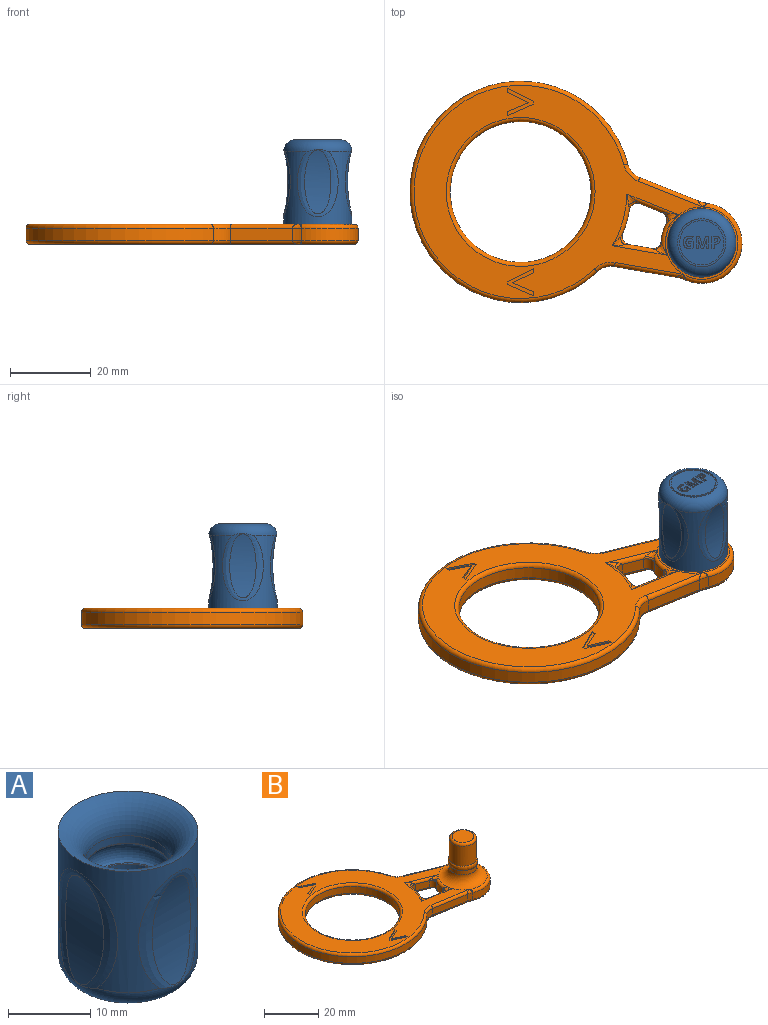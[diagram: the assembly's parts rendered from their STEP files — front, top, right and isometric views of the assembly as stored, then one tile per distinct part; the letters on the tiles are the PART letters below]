
ASSEMBLY  parts=2 mates=1
PART A: 79 faces, bbox 21x21x21.2 mm
  f0: cylinder r=5.2mm len=10.4mm, axis (0,0,1), area 36mm2, adj f14,f16
  f1: cylinder r=8.5mm len=18mm, axis (0,0,-1), area 388.7mm2, adj f6,f7,f8,f9,f10,f16
  f2: cylinder r=32.5mm len=15.91mm, axis (0,-1,0), area 83.7mm2, adj f6
  f3: cylinder r=32.5mm len=15.91mm, axis (0,-1,0), area 83.9mm2, adj f8
  f4: cylinder r=32.5mm len=15.92mm, axis (-1,0,0), area 83.9mm2, adj f7
  f5: cylinder r=32.5mm len=15.91mm, axis (-1,0,0), area 83.7mm2, adj f10
  f6: bspline ~17.38x10.13mm, area 57.8mm2, adj f1,f2,f9
  f7: bspline ~17.38x10.12mm, area 57.8mm2, adj f1,f4,f9
  f8: bspline ~17.38x10.12mm, area 58.2mm2, adj f1,f3,f9
  f9: torus R=5.5mm, axis (0,0,1), area 193.4mm2, adj f1,f6,f7,f8,f10,f18
  f10: bspline ~17.38x10.14mm, area 57.8mm2, adj f1,f5,f9
  f11: revolved ~11.8x11.8mm, area 116.4mm2, adj f14,f15
  f12: plane 10.4x10.4mm, normal (0,0,1), area 84.9mm2, adj f13
  f13: cylinder r=5.2mm len=10.45mm, axis (0,0,1), area 341.3mm2, adj f12,f15
  f14: torus R=5.35mm, axis (0,0,1), area 5.3mm2, adj f0,f11
  f15: torus R=5.35mm, axis (0,0,-1), area 5.3mm2, adj f11,f13
  f16: torus R=9.7mm, axis (0,0,1), area 234.1mm2, adj f0,f1
  f17: cylinder r=5.5mm len=11mm, axis (0,0,-1), area 13.8mm2, adj f19,f20
  f18: cylinder r=6mm len=12mm, axis (0,0,-1), area 13.5mm2, adj f9,f19
  f19: plane 12x12mm, normal (0,0,-1), area 18.1mm2, adj f17,f18
  f20: plane 11x11mm, normal (0,0,-1), area 80.4mm2, adj f17,f21,f22,f23,f24,f25,f26,f27
  f21: plane 1.18x0.4mm, normal (0,1,0), area 0.5mm2, adj f20,f22,f39,f40
  f22: plane 0.53x0.4mm, normal (1,0,0), area 0.2mm2, adj f20,f21,f23,f40
  f23: plane 0.56x0.4mm, normal (0,-1,0), area 0.2mm2, adj f20,f22,f24,f40
  f24: plane 0.62x0.4mm, normal (1,0,0), area 0.2mm2, adj f20,f23,f25,f40
  f25: extruded ~0.4x0.4mm, area 0.2mm2, adj f20,f24,f26,f40
  f26: extruded ~0.58x0.4mm, area 0.3mm2, adj f20,f25,f27,f40
  f27: extruded ~0.74x0.4mm, area 0.3mm2, adj f20,f26,f28,f40
  f28: extruded ~0.74x0.4mm, area 0.3mm2, adj f20,f27,f29,f40
  f29: extruded ~0.66x0.4mm, area 0.3mm2, adj f20,f28,f30,f40
  f30: extruded ~0.68x0.4mm, area 0.3mm2, adj f20,f29,f31,f40
  f31: plane 0.5x0.4mm, normal (-0.92,-0.38,0), area 0.2mm2, adj f20,f30,f32,f40
  f32: extruded ~0.88x0.4mm, area 0.4mm2, adj f20,f31,f33,f40
  f33: extruded ~1.14x0.4mm, area 0.5mm2, adj f20,f32,f34,f40
  f34: extruded ~1.12x0.41mm, area 0.5mm2, adj f20,f33,f35,f40
  f35: extruded ~1.14x0.4mm, area 0.5mm2, adj f20,f34,f36,f40
  f36: extruded ~1.03x0.4mm, area 0.5mm2, adj f20,f35,f37,f40
  f37: extruded ~0.52x0.4mm, area 0.2mm2, adj f20,f36,f38,f40
  f38: extruded ~0.54x0.4mm, area 0.2mm2, adj f20,f37,f39,f40
  f39: plane 1.54x0.4mm, normal (-1,0,0), area 0.6mm2, adj f20,f21,f38,f40
  f40: plane 3.06x2.44mm, normal (0,0,-1), area 4.3mm2, adj f21,f22,f23,f24,f25,f26,f27,f28
  f41: plane 2.33x0.72mm, normal (0.96,-0.29,0), area 1mm2, adj f20,f42,f59,f60
  f42: plane 0.58x0.4mm, normal (0,-1,0), area 0.2mm2, adj f20,f41,f43,f60
  f43: plane 2.33x0.77mm, normal (-0.95,-0.31,0), area 1mm2, adj f20,f42,f44,f60
  f44: plane 0.4x0.02mm, normal (0,-1,0), area 0mm2, adj f20,f43,f45,f60
  f45: extruded ~0.69x0.4mm, area 0.3mm2, adj f20,f44,f46,f60
  f46: extruded ~0.4x0.23mm, area 0.1mm2, adj f20,f45,f47,f60
  f47: plane 1.41x0.4mm, normal (1,0,0), area 0.6mm2, adj f20,f46,f48,f60
  f48: plane 0.59x0.4mm, normal (0,-1,0), area 0.2mm2, adj f20,f47,f49,f60
  f49: plane 2.97x0.4mm, normal (-1,0,0), area 1.2mm2, adj f20,f48,f50,f60
  f50: plane 0.86x0.4mm, normal (0,1,0), area 0.3mm2, adj f20,f49,f51,f60
  f51: plane 2.27x0.75mm, normal (0.95,0.31,0), area 1mm2, adj f20,f50,f52,f60
  f52: plane 0.4x0.01mm, normal (0,1,0), area 0mm2, adj f20,f51,f53,f60
  f53: plane 2.27x0.7mm, normal (-0.96,0.3,0), area 1mm2, adj f20,f52,f54,f60
  f54: plane 0.86x0.4mm, normal (0,1,0), area 0.3mm2, adj f20,f53,f55,f60
  f55: plane 2.97x0.4mm, normal (1,0,0), area 1.2mm2, adj f20,f54,f56,f60
  f56: plane 0.56x0.4mm, normal (0,-1,0), area 0.2mm2, adj f20,f55,f57,f60
  f57: plane 1.38x0.4mm, normal (-1,0,0), area 0.6mm2, adj f20,f56,f58,f60
  f58: extruded ~0.95x0.4mm, area 0.4mm2, adj f20,f57,f59,f60
  f59: plane 0.4x0.02mm, normal (0,-1,0), area 0mm2, adj f20,f41,f58,f60
  f60: plane 3.18x2.97mm, normal (0,0,-1), area 6.1mm2, adj f41,f42,f43,f44,f45,f46,f47,f48
  f61: extruded ~0.73x0.4mm, area 0.3mm2, adj f20,f62,f76,f77
  f62: extruded ~0.69x0.4mm, area 0.3mm2, adj f20,f61,f63,f77
  f63: extruded ~0.82x0.4mm, area 0.3mm2, adj f20,f62,f64,f77
  f64: plane 0.95x0.4mm, normal (0,1,0), area 0.4mm2, adj f20,f63,f65,f77
  f65: plane 2.97x0.4mm, normal (1,0,0), area 1.2mm2, adj f20,f64,f66,f77
  f66: plane 0.63x0.4mm, normal (0,-1,0), area 0.3mm2, adj f20,f65,f67,f77
  f67: plane 1.06x0.4mm, normal (-1,0,0), area 0.4mm2, adj f20,f66,f68,f77
  f68: plane 0.4x0.27mm, normal (0,-1,0), area 0.1mm2, adj f20,f67,f76,f77
  f69: plane 0.4x0.21mm, normal (0,1,0), area 0.1mm2, adj f70,f75,f77,f78
  f70: plane 0.88x0.4mm, normal (-1,0,0), area 0.4mm2, adj f69,f71,f77,f78
  f71: plane 0.4x0.29mm, normal (0,-1,0), area 0.1mm2, adj f70,f72,f77,f78
  f72: extruded ~0.4x0.38mm, area 0.2mm2, adj f71,f73,f77,f78
  f73: extruded ~0.4x0.33mm, area 0.1mm2, adj f72,f74,f77,f78
  f74: extruded ~0.4x0.33mm, area 0.2mm2, adj f73,f75,f77,f78
  f75: extruded ~0.44x0.4mm, area 0.2mm2, adj f69,f74,f77,f78
  f76: extruded ~0.85x0.4mm, area 0.4mm2, adj f20,f61,f68,f77
  f77: plane 2.97x2.05mm, normal (0,0,-1), area 3.6mm2, adj f61,f62,f63,f64,f65,f66,f67,f68
  f78: plane 0.88x0.79mm, normal (0,0,-1), area 0.6mm2, adj f69,f70,f71,f72,f73,f74,f75
PART B: 88 faces, bbox 87.6x59.5x23 mm
  f0: cylinder r=5mm len=13mm, axis (0,0,-1), area 394.6mm2, adj f24,f25,f86,f87
  f1: plane 71.67x53mm, normal (0,0,1), area 1242.5mm2, adj f24,f37,f39,f40,f41,f42,f43,f44
  f2: bspline ~2.83x2.45mm, area 2.5mm2, adj f34,f36,f61,f62
  f3: bspline ~2.83x2.45mm, area 2.5mm2, adj f45,f47,f62,f63
  f4: bspline ~2.54x2.25mm, area 1.8mm2, adj f35,f36,f58,f59
  f5: bspline ~2.54x2.25mm, area 1.8mm2, adj f46,f47,f59,f60
  f6: bspline ~2.81x2.09mm, area 1.8mm2, adj f33,f35,f55,f56
  f7: bspline ~2.81x2.09mm, area 1.8mm2, adj f44,f46,f56,f57
  f8: bspline ~2.86x2.45mm, area 2.5mm2, adj f33,f34,f52,f53
  f9: bspline ~2.86x2.45mm, area 2.5mm2, adj f44,f45,f53,f54
  f10: plane 45x45mm, normal (0,0,-1), area 511.7mm2, adj f32,f48,f49
  f11: cylinder r=10mm len=19.9mm, axis (0,0,-1), area 102.5mm2, adj f27,f38,f65,f68
  f12: plane 14.46x5.78mm, normal (0.37,0.93,0), area 46.7mm2, adj f13,f26,f37,f68
  f13: cylinder r=5mm len=3.38mm, axis (0,0,-1), area 14mm2, adj f12,f14,f28,f39
  f14: cylinder r=27.5mm len=55mm, axis (0,0,-1), area 430.7mm2, adj f13,f15,f30,f41
  f15: cylinder r=5mm len=4.31mm, axis (0,0,-1), area 14mm2, adj f14,f21,f31,f42
  f16: cylinder r=27.4mm len=5.86mm, axis (0,0,-1), area 18.3mm2, adj f34,f45,f53,f62
  f17: plane 5.36x3mm, normal (-0.37,-0.93,0), area 17.3mm2, adj f33,f44,f53,f56
  f18: cylinder r=10.1mm len=4.28mm, axis (0,0,-1), area 13.5mm2, adj f35,f46,f56,f59
  f19: cylinder r=17.5mm len=35mm, axis (0,0,-1), area 329.9mm2, adj f32,f43
  f20: plane 5.69x3mm, normal (0.17,0.99,0), area 17.3mm2, adj f36,f47,f59,f62
  f21: plane 15.34x3mm, normal (-0.17,-0.99,0), area 46.7mm2, adj f15,f29,f40,f65
  f22: plane 80.5x53mm, normal (0,0,-1), area 709.7mm2, adj f26,f27,f28,f29,f30,f31,f33,f34
  f23: plane 8x8mm, normal (0,0,1), area 50.3mm2, adj f25
  f24: torus R=9mm, axis (0,0,1), area 254.8mm2, adj f0,f1,f38
  f25: torus R=4mm, axis (0,0,1), area 45.8mm2, adj f0,f23
  f26: cylinder r=1mm len=16.32mm, axis (-0.93,0.37,0), area 25.7mm2, adj f12,f22,f28,f67
  f27: torus R=9mm, axis (0,0,1), area 53.5mm2, adj f11,f22,f64,f67
  f28: torus R=6mm, axis (0,0,1), area 7.9mm2, adj f13,f22,f26,f30
  f29: cylinder r=1mm len=17.1mm, axis (0.99,-0.17,0), area 25.7mm2, adj f21,f22,f31,f64
  f30: torus R=26.5mm, axis (0,0,1), area 222.5mm2, adj f14,f22,f28,f31
  f31: torus R=6mm, axis (0,0,1), area 7.9mm2, adj f15,f22,f29,f30
  f32: torus R=18.5mm, axis (0,0,1), area 176.3mm2, adj f10,f19
  f33: cylinder r=1mm len=13.23mm, axis (0.93,-0.37,0), area 13.9mm2, adj f6,f8,f17,f22,f52,f55
  f34: torus R=26.4mm, axis (0,0,1), area 14.1mm2, adj f2,f8,f16,f22,f52,f61
  f35: torus R=9.1mm, axis (0,0,1), area 11.1mm2, adj f4,f6,f18,f22,f55,f58
  f36: cylinder r=1mm len=13.82mm, axis (-0.99,0.17,0), area 13.9mm2, adj f2,f4,f20,f22,f58,f61
  f37: cylinder r=1mm len=16.32mm, axis (0.93,-0.37,0), area 25.7mm2, adj f1,f12,f39,f69
  f38: torus R=9mm, axis (0,0,1), area 53.5mm2, adj f11,f24,f66,f69
  f39: torus R=6mm, axis (0,0,1), area 7.9mm2, adj f1,f13,f37,f41
  f40: cylinder r=1mm len=17.1mm, axis (-0.99,0.17,0), area 25.7mm2, adj f1,f21,f42,f66
  f41: torus R=26.5mm, axis (0,0,1), area 222.5mm2, adj f1,f14,f39,f42
  f42: torus R=6mm, axis (0,0,1), area 7.9mm2, adj f1,f15,f40,f41
  f43: torus R=18.5mm, axis (0,0,1), area 176.3mm2, adj f1,f19
  f44: cylinder r=1mm len=13.23mm, axis (-0.93,0.37,0), area 13.9mm2, adj f1,f7,f9,f17,f54,f57
  f45: torus R=26.4mm, axis (0,0,1), area 14.1mm2, adj f1,f3,f9,f16,f54,f63
  f46: torus R=9.1mm, axis (0,0,1), area 11.1mm2, adj f1,f5,f7,f18,f57,f60
  f47: cylinder r=1mm len=13.82mm, axis (0.99,-0.17,0), area 13.9mm2, adj f1,f3,f5,f20,f60,f63
  f48: cylinder r=22.5mm len=45mm, axis (0,0,-1), area 276.7mm2, adj f10,f49,f51
  f49: cylinder r=1.5mm len=2.97mm, axis (0,0,-1), area 9.2mm2, adj f10,f48,f51
  f50: cylinder r=24.5mm len=49mm, axis (0,0,-1), area 307.9mm2, adj f22,f51
  f51: plane 49x49mm, normal (0,0,-1), area 298.8mm2, adj f48,f49,f50
  f52: bspline ~3.14x2.66mm, area 1.9mm2, adj f8,f33,f34
  f53: cylinder r=2mm len=3mm, axis (0,0,-1), area 10.7mm2, adj f8,f9,f16,f17
  f54: bspline ~3.14x2.66mm, area 1.9mm2, adj f9,f44,f45
  f55: bspline ~3.64x2.48mm, area 2.2mm2, adj f6,f33,f35
  f56: cylinder r=2mm len=3mm, axis (0,0,-1), area 10.1mm2, adj f6,f7,f17,f18
  f57: bspline ~3.64x2.48mm, area 2.2mm2, adj f7,f44,f46
  f58: bspline ~3.38x3.13mm, area 2.2mm2, adj f4,f35,f36
  f59: cylinder r=2mm len=3mm, axis (0,0,-1), area 10.1mm2, adj f4,f5,f18,f20
  f60: bspline ~3.38x3.13mm, area 2.2mm2, adj f5,f46,f47
  f61: bspline ~3.26x2.39mm, area 1.9mm2, adj f2,f34,f36
  f62: cylinder r=2mm len=3mm, axis (0,0,-1), area 10.7mm2, adj f2,f3,f16,f20
  f63: bspline ~3.26x2.39mm, area 1.9mm2, adj f3,f45,f47
  f64: bspline ~2.31x1.41mm, area 1.6mm2, adj f27,f29,f65
  f65: cylinder r=10mm len=3mm, axis (0,0,-1), area 7.3mm2, adj f11,f21,f64,f66
  f66: bspline ~2.31x1.41mm, area 1.6mm2, adj f38,f40,f65
  f67: bspline ~2.34x1.53mm, area 2.7mm2, adj f26,f27,f68
  f68: cylinder r=10mm len=3mm, axis (0,0,-1), area 7.3mm2, adj f11,f12,f67,f69
  f69: bspline ~2.34x1.53mm, area 1.6mm2, adj f37,f38,f68
  f70: plane 5.31x2.21mm, normal (0.38,-0.92,0), area 2.3mm2, adj f1,f71,f76,f77
  f71: plane 1.02x0.4mm, normal (1,0,0), area 0.4mm2, adj f1,f70,f72,f77
  f72: plane 6.52x2.86mm, normal (-0.4,0.92,0), area 2.8mm2, adj f1,f71,f73,f77
  f73: plane 0.66x0.4mm, normal (-1,0,0), area 0.3mm2, adj f1,f72,f74,f77
  f74: plane 6.52x3.25mm, normal (-0.45,-0.89,0), area 2.9mm2, adj f1,f73,f75,f77
  f75: plane 1.01x0.4mm, normal (1,0,0), area 0.4mm2, adj f1,f74,f76,f77
  f76: plane 5.31x2.53mm, normal (0.43,0.9,0), area 2.4mm2, adj f1,f70,f75,f77
  f77: plane 6.78x6.52mm, normal (0,0,1), area 11.7mm2, adj f70,f71,f72,f73,f74,f75,f76
  f78: plane 6.52x2.86mm, normal (0.4,0.92,0), area 2.8mm2, adj f1,f79,f84,f85
  f79: plane 1.02x0.4mm, normal (-1,0,0), area 0.4mm2, adj f1,f78,f80,f85
  f80: plane 5.3x2.22mm, normal (-0.39,-0.92,0), area 2.3mm2, adj f1,f79,f81,f85
  f81: plane 5.3x2.52mm, normal (-0.43,0.9,0), area 2.3mm2, adj f1,f80,f82,f85
  f82: plane 1.01x0.4mm, normal (-1,0,0), area 0.4mm2, adj f1,f81,f83,f85
  f83: plane 6.52x3.25mm, normal (0.45,-0.89,0), area 2.9mm2, adj f1,f82,f84,f85
  f84: plane 0.66x0.4mm, normal (1,0,0), area 0.3mm2, adj f1,f78,f83,f85
  f85: plane 6.78x6.52mm, normal (0,0,1), area 11.7mm2, adj f78,f79,f80,f81,f82,f83,f84
  f86: cylinder r=5.05mm len=10.09mm, axis (0,0,1), area 49.6mm2, adj f0,f87
  f87: revolved ~10.85x10.85mm, area 77mm2, adj f0,f86
PLACE A rot(axis=(-1,0,0),180deg) t=(34.42,23.96,48.82)mm
PLACE B t=(-10.58,36.63,22.82)mm fixed
MATE revolute B.f86 <-> A.f14  axis (0,0,1) through (34.42,23.96,34.82)mm
